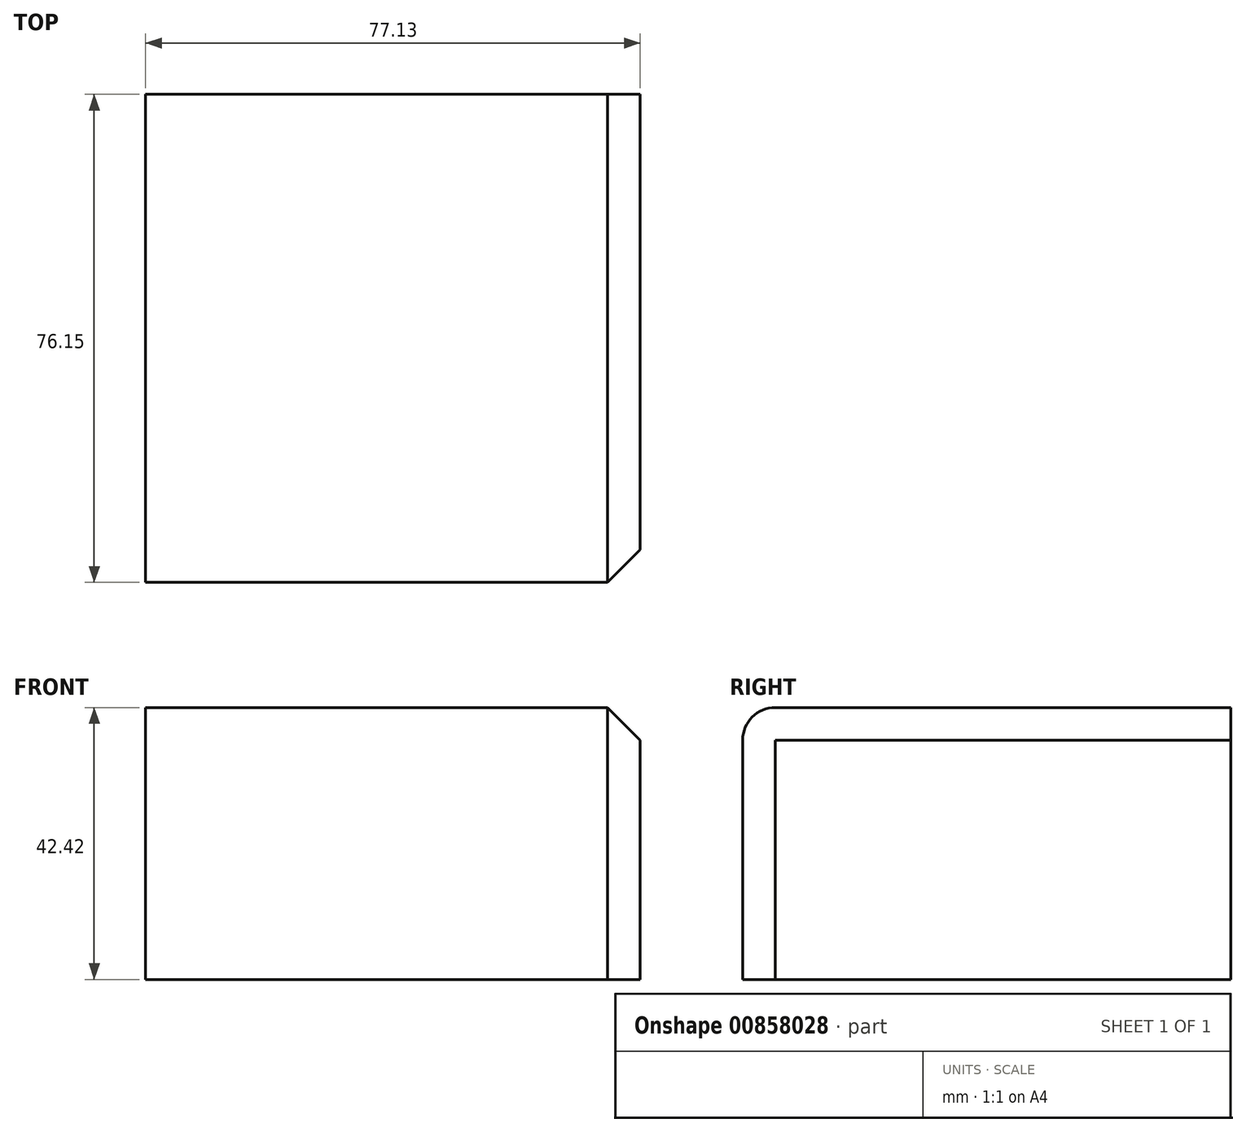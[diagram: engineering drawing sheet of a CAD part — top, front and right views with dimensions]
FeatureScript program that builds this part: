
annotation { "Feature Type Name" : "Feature", "Feature Type Description" : "" }
export const myFeature = defineFeature(function(context is Context, id is Id, definition is map)
    precondition{}
    {
        {
            var Q0;
            Q0=qCreatedBy(makeId("Top.planeOp"),FACE);
            var sketch = newSketch(context, id + "F0", { "sketchPlane" : qUnion([Q0])});
            skLineSegment(sketch, "E0.bottom", {"start": v(0, 0) * mm, "end": v(77.13, 0) * mm});
            skLineSegment(sketch, "E0.top", {"start": v(0, 76.15) * mm, "end": v(77.13, 76.15) * mm});
            skLineSegment(sketch, "E0.left", {"start": v(0, 0) * mm, "end": v(0, 76.15) * mm});
            skLineSegment(sketch, "E0.right", {"start": v(77.13, 0) * mm, "end": v(77.13, 76.15) * mm});
            skSolve(sketch);
        }
        {
            var Q0;
            Q0 = qSketchRegion(id + "F0", true);
            extrude(context, id + "F1", {"entities" : qUnion([Q0]), "depth" : 42.42 * mm, "offsetDistance" : 25.4 * mm});
        }
        {
            var Q0;
            Q0=makeQuery(id+"F1.opExtrude","CAP_EDGE",EDGE,{"disambiguationData":[OSD([sQuery(id+"F0.wireOp",EDGE,"E0.bottom")])],"isStart":false});
            fillet(context, id + "F2", {"entities" : qUnion([Q0]), "radius" : 5.08 * mm, "tangentPropagation" : true, "allowEdgeOverflow" : false});
        }
        {
            var Q0;
            Q0=makeQuery(id+"F1.opExtrude","CAP_EDGE",EDGE,{"disambiguationData":[OSD([sQuery(id+"F0.wireOp",EDGE,"E0.right")])],"isStart":false});
            chamfer(context, id + "F3", {"entities" : qUnion([Q0]), "width" : 5.08 * mm, "tangentPropagation" : true});
        }
    });
